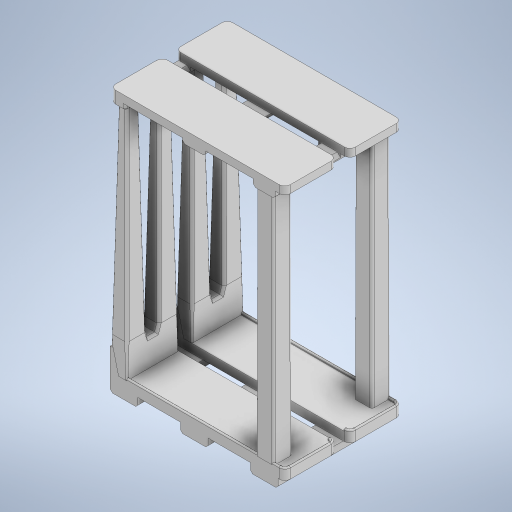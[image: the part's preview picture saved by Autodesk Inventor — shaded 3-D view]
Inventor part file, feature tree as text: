
AUTODESK INVENTOR PART (.ipt)
format: ipt  version: 2024.1 (Build 281209000, 209)  size: 1,487,360 bytes
history: native  units: mm
features: projected_geometry x43, extrude x23, sketch x23, chamfer x8, fillet x6, other x4, pattern_linear x1
ambient origin geometry x8: Origin, YZ Plane, XZ Plane, XY Plane, X Axis, Y Axis, Z Axis, Center Point
bodies: Body1 (feature_tree), Body2 (feature_tree), Body3 (feature_tree), Body4 (feature_tree)
feature tree (108):
  other  "span"
  extrude  "Extrusion1"  Depth=6.0mm
  extrude  "Extrusion2"  Depth=47.0mm
  sketch  "Sketch3"  dims[d4=158.0mm d5=8.0mm d6=0.0mm d7=152.0mm]
  sketch  "Sketch4"  dims[d8=25.0mm d9=25.0mm]
  extrude  "Extrusion4"  Depth=8.0mm TaperAngle=0.0deg
  fillet  "Fillet1"  Radius=152.0mm
  extrude  "Extrusion3"  Depth=25.0mm
  chamfer  "Chamfer1"  Distance=8.0mm
  fillet  "Fillet2"  Radius=15.0mm
  extrude  "Extrusion5"  Depth=17.0mm
  extrude  "Extrusion6"  Depth=220.0mm
  pattern_linear  "Rectangular Pattern1"  Count1=2 Spacing1=0.0mm
  fillet  "Fillet3"  Radius=2.5mm
  chamfer  "Chamfer2"  Distance=2.0mm Angle=45.0deg
  chamfer  "Chamfer3"  Distance=2.0mm Angle=45.0deg
  extrude  "Extrusion7"  Depth=2.5mm
  fillet  "Fillet4"  Radius=2.0mm
  extrude  "Extrusion9"  Depth=14.5mm
  extrude  "Extrusion10"  Depth=30.0mm TaperAngle=0.0deg
  sketch  "Sketch10"  dims[d21=14.0mm]
  extrude  "Extrusion11"  Depth=10.0mm TaperAngle=0.0deg
  extrude  "Extrusion12"  Depth=10.0mm TaperAngle=0.0deg
  extrude  "Extrusion13"  Depth=10.0mm TaperAngle=0.0deg
  extrude  "Extrusion14"  Depth=10.0mm TaperAngle=0.0deg
  extrude  "Extrusion15"  Depth=18.0mm
  extrude  "Extrusion16"  Depth=2.0mm
  extrude  "Extrusion17"  Depth=18.0mm
  chamfer  "Chamfer4"  Distance=18.0mm
  extrude  "Extrusion18"  Depth=18.0mm
  extrude  "Extrusion19"  Depth=10.0mm
  extrude  "Extrusion20"  Depth=6.0mm
  extrude  "Extrusion21"  Depth=2.0mm
  fillet  "Fillet5"  Radius=2.0mm
  fillet  "Fillet6"  Radius=2.0mm
  extrude  "Extrusion22"  Depth=2.0mm
  extrude  "Extrusion23"  TaperAngle=0.0deg  [1 undecoded]
  chamfer  "Chamfer5"  Distance=2.0mm Angle=45.0deg
  chamfer  "Chamfer6"  Distance=0.6mm
  chamfer  "Chamfer7"  Distance=0.6mm
  extrude  "Extrusion24"  Depth=10.0mm TaperAngle=0.0deg
  chamfer  "Chamfer8"  Distance=0.6mm
  sketch  "Sketch1"  dims[d0=6.0mm d1=6.0mm]
  sketch  "Sketch2"  dims[d2=47.0mm d3=47.0mm]
  projected_geometry  "Projected Loop1"
  other  "leggie-boys"
  sketch  "Sketch5"  dims[d10=25.0mm]
  projected_geometry  "Projected Loop2"
  projected_geometry  "Projected Loop3"
  sketch  "Sketch6"  dims[d11=38.5mm]
  projected_geometry  "Projected Loop4"
  sketch  "Sketch7"  dims[d12=38.5mm d13=8.0mm d14=0.0mm d15=15.0mm]
  projected_geometry  "Projected Loop5"
  projected_geometry  "Projected Loop6"
  sketch  "Sketch8"  dims[d16=17.0mm d17=17.0mm]
  projected_geometry  "Projected Loop7"
  projected_geometry  "Projected Loop8"
  sketch  "Sketch9"  dims[d18=17.0mm d19=220.0mm d20=-0.017453mm]
  projected_geometry  "Projected Loop9"
  other  "back-leggies"
  projected_geometry  "Projected Loop10"
  projected_geometry  "Projected Loop11"
  sketch  "Sketch11"  dims[d22=14.0mm]
  projected_geometry  "Projected Loop12"
  projected_geometry  "Projected Loop13"
  sketch  "Sketch12"  dims[d23=10.0mm]
  projected_geometry  "Projected Loop14"
  projected_geometry  "Projected Loop15"
  projected_geometry  "Projected Loop16"
  projected_geometry  "Projected Loop17"
  projected_geometry  "Projected Loop18"
  projected_geometry  "Projected Loop19"
  projected_geometry  "Projected Loop20"
  sketch  "Sketch13"  dims[d24=15.0mm d25=-0.349066mm]
  projected_geometry  "Projected Loop21"
  projected_geometry  "Projected Loop22"
  sketch  "Sketch14"  dims[d26=4.0mm]
  projected_geometry  "Projected Loop23"
  projected_geometry  "Projected Loop24"
  projected_geometry  "Projected Loop25"
  projected_geometry  "Projected Loop26"
  sketch  "Sketch15"  dims[d27=4.0mm]
  sketch  "Sketch16"  dims[d28=2.0mm]
  sketch  "Sketch17"  dims[d29=2.0mm d30=2.0mm d31=45.0deg]
  projected_geometry  "Projected Loop27"
  projected_geometry  "Projected Loop28"
  sketch  "Sketch18"  dims[d32=2.0mm d33=20.0mm d34=0.0mm d35=2.5mm d36=0.0mm]
  projected_geometry  "Projected Loop29"
  projected_geometry  "Projected Loop30"
  projected_geometry  "Projected Loop31"
  projected_geometry  "Projected Loop32"
  sketch  "Sketch19"  dims[d37=20.0mm d39=59.0mm d40=20.0mm d42=44.5mm]
  sketch  "Sketch20"  dims[d43=5.0mm d44=2.0mm d45=2.0mm d46=45.0deg d47=2.0mm d48=2.0mm d49=45.0deg]
  other  "hattie-boy"
  sketch  "Sketch22"  dims[d50=2.5mm d51=2.5mm d52=2.0mm d53=0.0mm]
  projected_geometry  "Projected Loop34"
  projected_geometry  "Projected Loop35"
  projected_geometry  "Projected Loop36"
  projected_geometry  "Projected Loop37"
  projected_geometry  "Projected Loop38"
  projected_geometry  "Projected Loop39"
  projected_geometry  "Projected Loop40"
  projected_geometry  "Projected Loop41"
  sketch  "Sketch23"  dims[d54=1.2mm d57=14.5mm d58=-0.349066mm]
  projected_geometry  "Projected Loop42"
  projected_geometry  "Projected Loop43"
  sketch  "Sketch25"  dims[d59=14.5mm d60=-0.349066mm d61=30.0mm d62=0.0mm d63=10.0mm d64=0.0mm d65=10.0mm d66=0.0mm d67=10.0mm d68=0.0mm d69=10.0mm d70=0.0mm d71=18.0mm d72=15.0mm d73=18.0mm d74=18.0mm d75=18.0mm d76=10.0mm d77=-0.174533mm d78=6.0mm d79=2.0mm d80=2.0mm d83=2.0mm d84=2.0mm d85=0.0mm d86=0.0mm d87=2.0mm d88=2.0mm d89=45.0deg d90=0.6mm d91=0.6mm d92=10.0mm d93=0.0mm d94=0.6mm d95=10.0mm d96=0.0mm d97=3.0mm d98=0.0mm d99=3.0mm d100=0.0mm d101=1.0mm d102=5.0mm d103=4.0mm d104=0.0mm d105=2.5mm d106=2.5mm d107=2.5mm d108=4.0mm d109=0.0mm d110=3.0mm d111=2.0mm d112=45.0deg d113=3.0mm d114=2.0mm d115=45.0deg d116=2.0mm d117=2.0mm d118=45.0deg d121=4.0mm d122=0.0mm d123=2.0mm d124=2.0mm d125=45.0deg]
  projected_geometry  "Projected Loop46"
note: 1 required parameter value undecoded (feature->parameter linkage not recoverable at this tier; creation-order binding heuristic only, values carry confidence <= 0.55)
